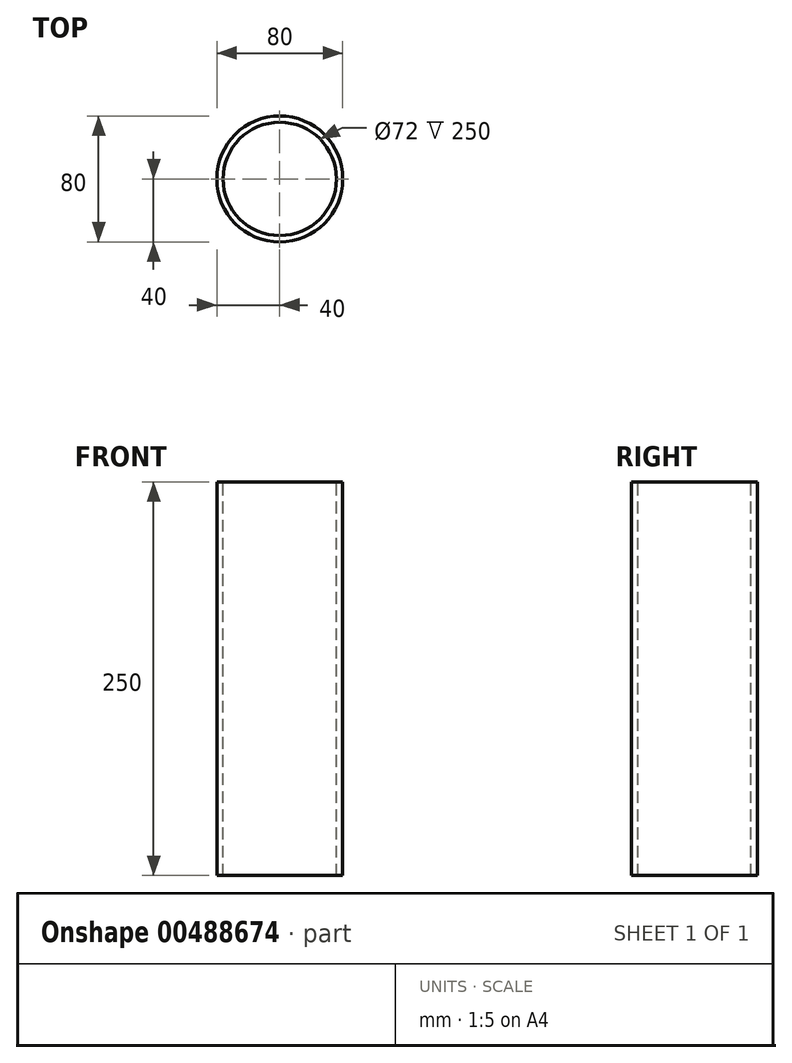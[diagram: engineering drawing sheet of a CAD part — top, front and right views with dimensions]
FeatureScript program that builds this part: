
annotation { "Feature Type Name" : "Feature", "Feature Type Description" : "" }
export const myFeature = defineFeature(function(context is Context, id is Id, definition is map)
    precondition{}
    {
        {
            var Q0;
            Q0=qCreatedBy(makeId("Top.planeOp"),FACE);
            var sketch = newSketch(context, id + "F0", { "sketchPlane" : qUnion([Q0])});
            skCircle(sketch, "E0", {"center": v(0, 0) * mm, "radius": 40 * mm});
            skCircle(sketch, "E1", {"center": v(0, 0) * mm, "radius": 36 * mm});
            skSolve(sketch);
        }
        {
            var Q0;
            Q0=makeQuery(id+"F0.imprint","IMPRINT",FACE,{"disambiguationData":[TD([[makeQuery(id+"F0.imprint","IMPRINT",EDGE,{"derivedFrom":sQuery(id+"F0.wireOp",EDGE,"E0")}),1.0]])]});
            extrude(context, id + "F1", {"entities" : qUnion([Q0]), "oppositeDirection" : true, "depth" : (250 / 2) * mm, "hasSecondDirection" : true, "secondDirectionOppositeDirection" : false, "secondDirectionDepth" : (250 / 2) * mm});
        }
    });
